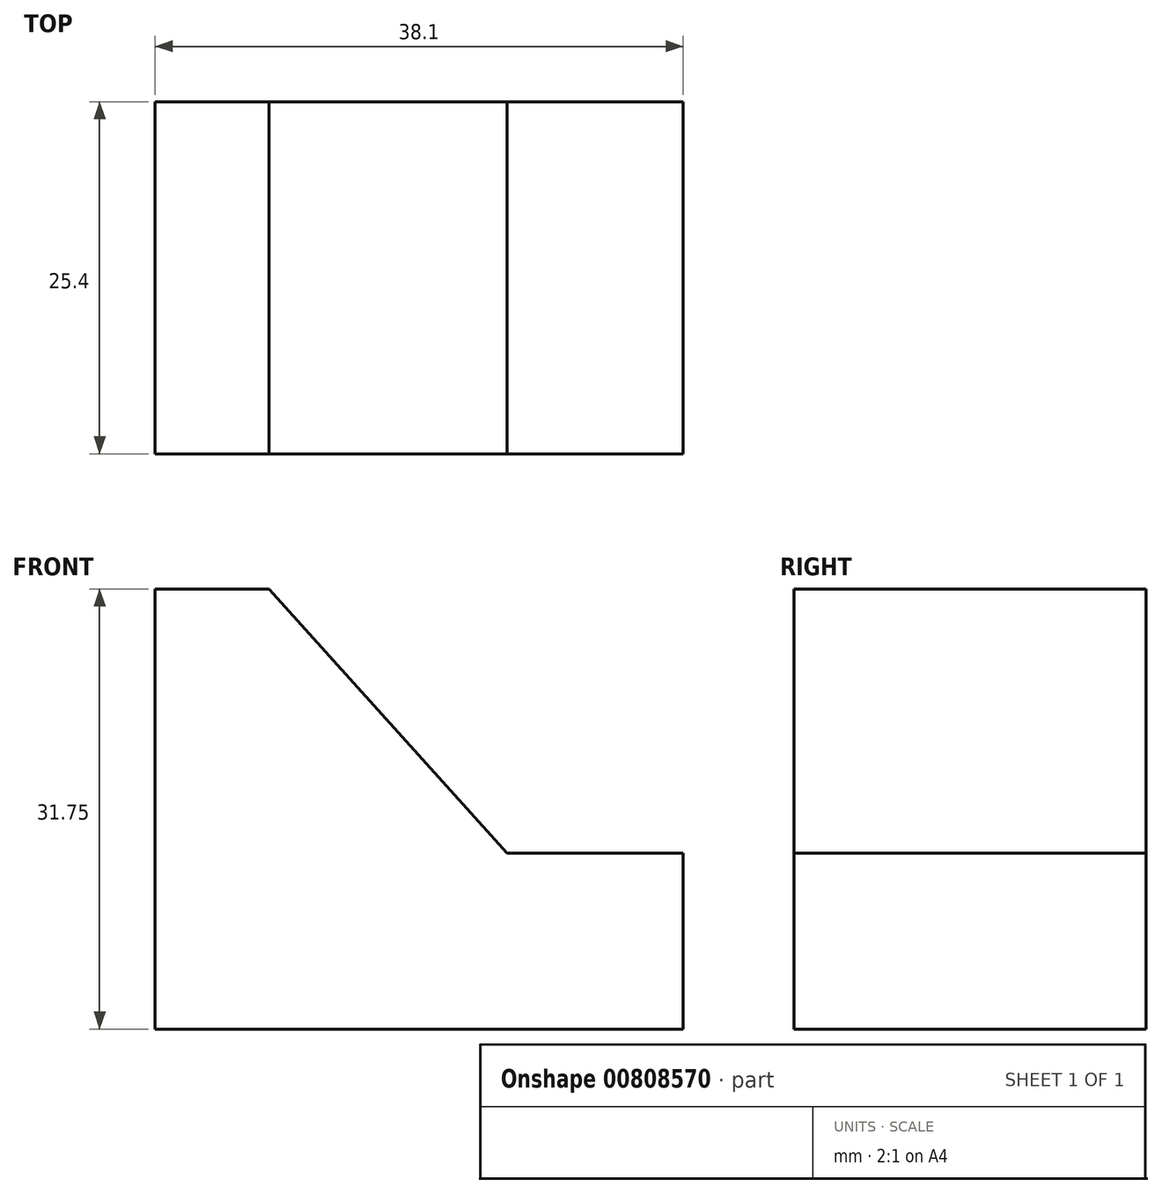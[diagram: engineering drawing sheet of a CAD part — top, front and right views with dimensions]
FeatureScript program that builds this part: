
annotation { "Feature Type Name" : "Feature", "Feature Type Description" : "" }
export const myFeature = defineFeature(function(context is Context, id is Id, definition is map)
    precondition{}
    {
        {
            var Q0;
            Q0=qCreatedBy(makeId("Front.planeOp"),FACE);
            var sketch = newSketch(context, id + "F0", { "sketchPlane" : qUnion([Q0])});
            skLineSegment(sketch, "E0", {"start": v(0, 0) * mm, "end": v(0, 31.75) * mm});
            skLineSegment(sketch, "E1", {"start": v(0, 31.75) * mm, "end": v(8.22, 31.75) * mm});
            skLineSegment(sketch, "E2", {"start": v(0, 0) * mm, "end": v(38.1, 0) * mm});
            skLineSegment(sketch, "E3", {"start": v(38.1, 0) * mm, "end": v(38.1, 12.7) * mm});
            skLineSegment(sketch, "E4", {"start": v(38.1, 12.7) * mm, "end": v(25.4, 12.7) * mm});
            skLineSegment(sketch, "E5", {"start": v(8.22, 31.75) * mm, "end": v(25.4, 12.7) * mm});
            skSolve(sketch);
        }
        {
            var Q0;
            Q0 = qSketchRegion(id + "F0", true);
            extrude(context, id + "F1", {"entities" : qUnion([Q0]), "depth" : 25.4 * mm, "offsetDistance" : 25.4 * mm});
        }
    });
